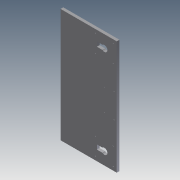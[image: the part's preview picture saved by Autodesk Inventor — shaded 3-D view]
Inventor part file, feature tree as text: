
AUTODESK INVENTOR PART (.ipt)
format: ipt  version: 2011 (Build 150239000, 239)  size: 501,248 bytes
history: native  units: in
note: dims shown in document units (in); Inventor stores cm internally (conversion verified against a paired STEP export)
features: extrude x47, sketch x47, fillet x1
ambient origin geometry x8: Origin, YZ Plane, XZ Plane, XY Plane, X Axis, Y Axis, Z Axis, Center Point
bodies: Solid1 (feature_tree)
feature tree (95):
  extrude  "Extrusion1"  Depth=4.0in
  extrude  "Extrusion2"  Depth=2.16in
  extrude  "Extrusion3"  Depth=1.7655in
  extrude  "Extrusion4"  Depth=0.029in TaperAngle=0.0deg
  extrude  "Extrusion5"  Depth=2.36in
  fillet  "Fillet1"  Radius=2.56in
  extrude  "Extrusion6"  Depth=0.125in
  extrude  "Extrusion7"  Depth=0.262in TaperAngle=0.0deg
  extrude  "Extrusion8"  Depth=0.029in TaperAngle=0.0deg
  extrude  "Extrusion9"  Depth=0.156in
  extrude  "Extrusion10"  Depth=0.5in TaperAngle=0.0deg
  extrude  "Extrusion11"  Depth=0.5in TaperAngle=0.0deg
  extrude  "Extrusion12"  Depth=1.875in TaperAngle=0.0deg
  extrude  "Extrusion13"  Depth=2.125in TaperAngle=0.0deg
  sketch  "Sketch14"  dims[d44=2.125in d45=0.0in d46=2.125in d47=0.0in]
  sketch  "Sketch15"  dims[d48=2.125in d49=0.0in d50=1.875in d51=0.0in]
  sketch  "Sketch16"  dims[d52=2.125in d53=0.0in d54=2.125in d55=0.0in]
  sketch  "Sketch17"  dims[d56=1.875in d57=0.0in d58=1.875in d59=0.0in]
  extrude  "Extrusion14"  Depth=2.125in TaperAngle=0.0deg
  extrude  "Extrusion15"  Depth=1.875in TaperAngle=0.0deg
  extrude  "Extrusion16"  Depth=2.125in TaperAngle=0.0deg
  extrude  "Extrusion17"  Depth=1.875in TaperAngle=0.0deg
  extrude  "Extrusion18"  Depth=2.125in TaperAngle=0.0deg
  extrude  "Extrusion19"  Depth=6.248in TaperAngle=0.0deg
  extrude  "Extrusion20"  Depth=1.281in
  extrude  "Extrusion21"  Depth=7.0in TaperAngle=0.0deg
  extrude  "Extrusion22"  Depth=0.25in TaperAngle=0.0deg
  extrude  "Extrusion23"  Depth=0.25in TaperAngle=0.0deg
  extrude  "Extrusion24"  Depth=0.25in TaperAngle=0.0deg
  extrude  "Extrusion25"  Depth=0.25in TaperAngle=0.0deg
  extrude  "Extrusion26"  Depth=0.875in
  extrude  "Extrusion27"  Depth=0.875in
  extrude  "Extrusion28"  Depth=1.0in TaperAngle=0.0deg
  extrude  "Extrusion29"  Depth=0.5in TaperAngle=0.0deg
  extrude  "Extrusion30"  Depth=0.4134in
  extrude  "Extrusion31"  Depth=0.8268in
  extrude  "Extrusion32"  Depth=0.8268in
  extrude  "Extrusion33"  Depth=0.9055in
  extrude  "Extrusion34"  Depth=1.1024in
  extrude  "Extrusion35"  Depth=1.0in TaperAngle=0.0deg
  extrude  "Extrusion36"  Depth=3.0in
  extrude  "Extrusion37"  Depth=0.5in
  extrude  "Extrusion38"  Depth=0.5in
  extrude  "Extrusion39"  Depth=0.75in
  extrude  "Extrusion40"  Depth=0.75in
  extrude  "Extrusion41"  Depth=0.156in
  extrude  "Extrusion42"  Depth=1.0in TaperAngle=0.0deg
  extrude  "Extrusion43"  Depth=1.0in
  extrude  "Extrusion44"  [1 undecoded]
  extrude  "Extrusion45"  [1 undecoded]
  extrude  "Extrusion46"  [1 undecoded]
  extrude  "Extrusion47"  [1 undecoded]
  sketch  "Sketch1"  dims[d0=4.0in d1=4.0in]
  sketch  "Sketch2"  dims[d2=0.029in d3=0.0in d4=2.16in]
  sketch  "Sketch3"  dims[d5=0.029in d6=0.0in d7=1.7655in]
  sketch  "Sketch4"  dims[d8=0.156in d9=0.029in d10=0.0in]
  sketch  "Sketch5"  dims[d11=0.029in d12=0.0in d13=2.36in d14=2.56in]
  sketch  "Sketch6"  dims[d15=0.262in d16=0.0in d17=0.125in]
  sketch  "Sketch7"  dims[d18=0.362in d19=0.0in d20=0.262in d21=0.0in]
  sketch  "Sketch8"  dims[d22=0.1in d23=0.0in d24=0.029in d25=0.0in]
  sketch  "Sketch9"  dims[d26=1.594in d27=0.156in]
  sketch  "Sketch10"  dims[d28=0.029in d29=0.0in d30=0.5in d31=0.0in]
  sketch  "Sketch11"  dims[d32=0.75in d33=0.0in d34=0.5in d35=0.0in]
  sketch  "Sketch12"  dims[d36=2.125in d37=0.0in d38=1.875in d39=0.0in]
  sketch  "Sketch13"  dims[d40=1.875in d41=0.0in d42=2.125in d43=0.0in]
  sketch  "Sketch18"  dims[d60=2.125in d61=0.0in d62=2.125in d63=0.0in]
  sketch  "Sketch19"  dims[d64=0.875in d65=0.0in d66=6.248in d67=0.0in]
  sketch  "Sketch20"  dims[d68=7.0in d69=0.0in d70=1.281in]
  sketch  "Sketch21"  dims[d71=3.188in d72=7.0in d73=0.0in]
  sketch  "Sketch22"  dims[d74=0.25in d75=0.0in d76=0.25in d77=0.0in]
  sketch  "Sketch23"  dims[d78=0.25in d79=0.0in d80=0.25in d81=0.0in]
  sketch  "Sketch24"  dims[d82=0.25in d83=0.0in d84=0.25in d85=0.0in]
  sketch  "Sketch25"  dims[d86=3.875in d87=0.0in d88=0.25in d89=0.0in]
  sketch  "Sketch26"  dims[d90=0.25in d91=0.0in d92=0.875in]
  sketch  "Sketch27"  dims[d93=0.875in d94=0.875in]
  sketch  "Sketch28"  dims[d95=0.875in d96=1.0in d97=0.0in]
  sketch  "Sketch29"  dims[d98=0.25in d99=0.0in d100=0.5in d101=0.0in]
  sketch  "Sketch30"  dims[d102=0.8858in d103=0.4134in]
  sketch  "Sketch31"  dims[d104=1.378in d105=0.8268in]
  sketch  "Sketch32"  dims[d106=0.4134in d107=0.8268in]
  sketch  "Sketch33"  dims[d108=0.9055in d109=0.9055in]
  sketch  "Sketch34"  dims[d110=0.5in d111=0.0in d112=1.1024in]
  sketch  "Sketch35"  dims[d113=1.1024in d114=1.0in d115=0.0in]
  sketch  "Sketch36"  dims[d116=2.75in d117=3.0in]
  sketch  "Sketch37"  dims[d118=5.5in d119=0.5in]
  sketch  "Sketch38"  dims[d120=0.5in d121=0.5in]
  sketch  "Sketch39"  dims[d122=0.5in d123=0.75in]
  sketch  "Sketch40"  dims[d124=0.75in d125=0.75in]
  sketch  "Sketch41"  dims[d126=0.75in d127=0.156in]
  sketch  "Sketch42"  dims[d128=0.156in d129=1.0in d130=0.0in]
  sketch  "Sketch43"  dims[d131=5.0in d132=1.0in]
  sketch  "Sketch44"  dims[d133=1.0in d134=0.0in]
  sketch  "Sketch45"
  sketch  "Sketch46"
  sketch  "Sketch47"
note: 4 required parameter values undecoded (feature->parameter linkage not recoverable at this tier; creation-order binding heuristic only, values carry confidence <= 0.55)
